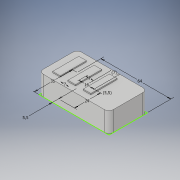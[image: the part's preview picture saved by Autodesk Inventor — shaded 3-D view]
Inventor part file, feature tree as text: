
AUTODESK INVENTOR PART (.ipt)
format: ipt  version: 2019 (Build 230136000, 136)  size: 135,168 bytes
history: native  units: mm
features: extrude x2, sketch x1, fillet x1
ambient origin geometry x8: Origin, YZ Plane, XZ Plane, XY Plane, X Axis, Y Axis, Z Axis, Center Point
bodies: Solid1 (feature_tree)
feature tree (4):
  sketch  "Sketch1"  dims[d0=35.0mm d1=64.0mm d2=7.0mm d3=7.0mm d4=24.0mm d5=5.5mm d6=5.5mm d7=30.0mm d9=14.0mm d10=10.0mm d12=10.0mm d14=7.0mm d15=18.0mm d16=0.0mm d17=19.0mm d18=0.0mm d19=4.0mm]
  extrude  "Extrusion1"  Depth=64.0mm
  extrude  "Extrusion2"  Depth=7.0mm
  fillet  "Fillet1"  Radius=7.0mm
